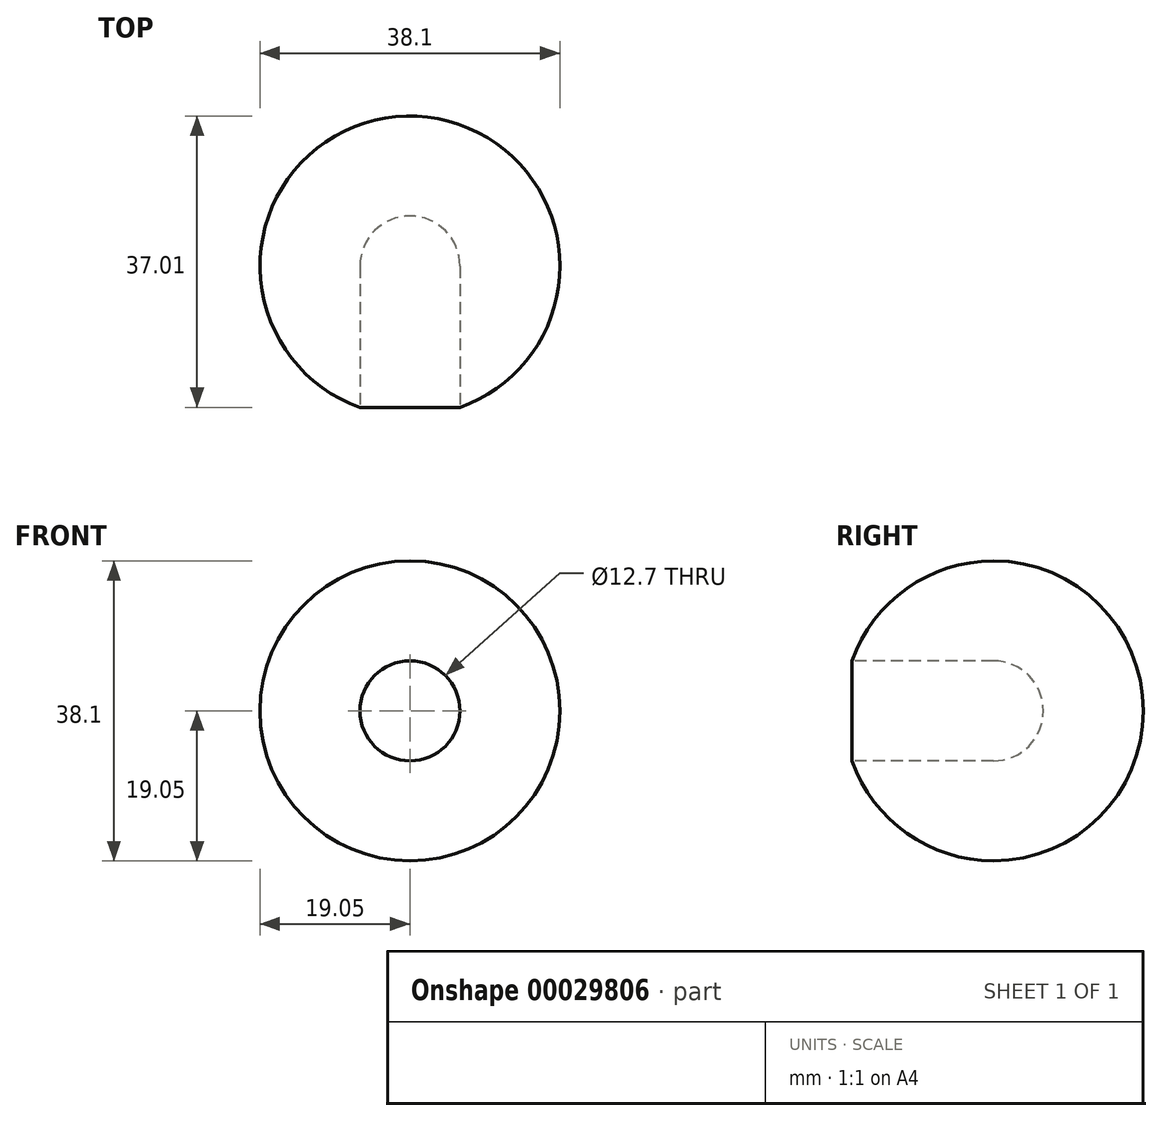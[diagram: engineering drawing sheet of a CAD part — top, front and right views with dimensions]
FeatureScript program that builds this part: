
annotation { "Feature Type Name" : "Feature", "Feature Type Description" : "" }
export const myFeature = defineFeature(function(context is Context, id is Id, definition is map)
    precondition{}
    {
        {
            var Q0;
            Q0=qCreatedBy(makeId("Front.planeOp"),FACE);
            var sketch = newSketch(context, id + "F0", { "sketchPlane" : qUnion([Q0])});
            skCircle(sketch, "E0", {"center": v(0, 0) * mm, "radius": 19.05 * mm});
            skLineSegment(sketch, "E1", {"start": v(0, 19.05) * mm, "end": v(0, -19.05) * mm});
            skCircle(sketch, "E2", {"center": v(0, 0) * mm, "radius": 6.35 * mm});
            skSolve(sketch);
        }
        {
            var Q0;
            {var subQ1=sQuery(id+"F0.wireOp",EDGE,"E1");var subQ4=sQuery(id+"F0.wireOp",EDGE,"E0");var subQ6=makeQuery(id+"F0.imprint","INTERSECT",VERTEX,{"disambiguationData":[OD(0.0)],"derivedFrom":[subQ4,subQ1]});Q0=makeQuery(id+"F0.imprint","IMPRINT",FACE,{"disambiguationData":[TD([[makeQuery(id+"F0.imprint","IMPRINT",EDGE,{"disambiguationData":[TD([[subQ6,1.0]])],"derivedFrom":subQ4}),1.0]])]});}
            var Q1;
            Q1=sQuery(id+"F0.wireOp",EDGE,"E1");
            revolve(context, id + "F1", {"entities" : qUnion([Q0]), "axis" : qUnion([Q1]), "revolveType" : RevolveType.FULL});
        }
        {
            var Q0;
            Q0=qCreatedBy(makeId("Front.planeOp"),FACE);
            cPlane(context, id + "F2", {"entities" : qUnion([Q0]), "cplaneType" : CPlaneType.OFFSET, "offset" : 19.05 * mm, "width" : 152.4 * mm, "height" : 152.4 * mm});
        }
        {
            var Q0;
            Q0=qCreatedBy(id+"F2.planeOp",FACE);
            var sketch = newSketch(context, id + "F3", { "sketchPlane" : qUnion([Q0])});
            skCircle(sketch, "E3", {"center": v(0, 0) * mm, "radius": 6.35 * mm});
            skSolve(sketch);
        }
        {
            var Q0;
            Q0=makeQuery(id+"F3.imprint","IMPRINT",FACE,{"disambiguationData":[TD([[makeQuery(id+"F3.imprint","IMPRINT",EDGE,{"derivedFrom":sQuery(id+"F3.wireOp",EDGE,"E3")}),1.0]])]});
            extrude(context, id + "F4", {"entities" : qUnion([Q0]), "operationType" : NewBodyOperationType.REMOVE, "oppositeDirection" : true, "depth" : 19.05 * mm});
        }
    });
